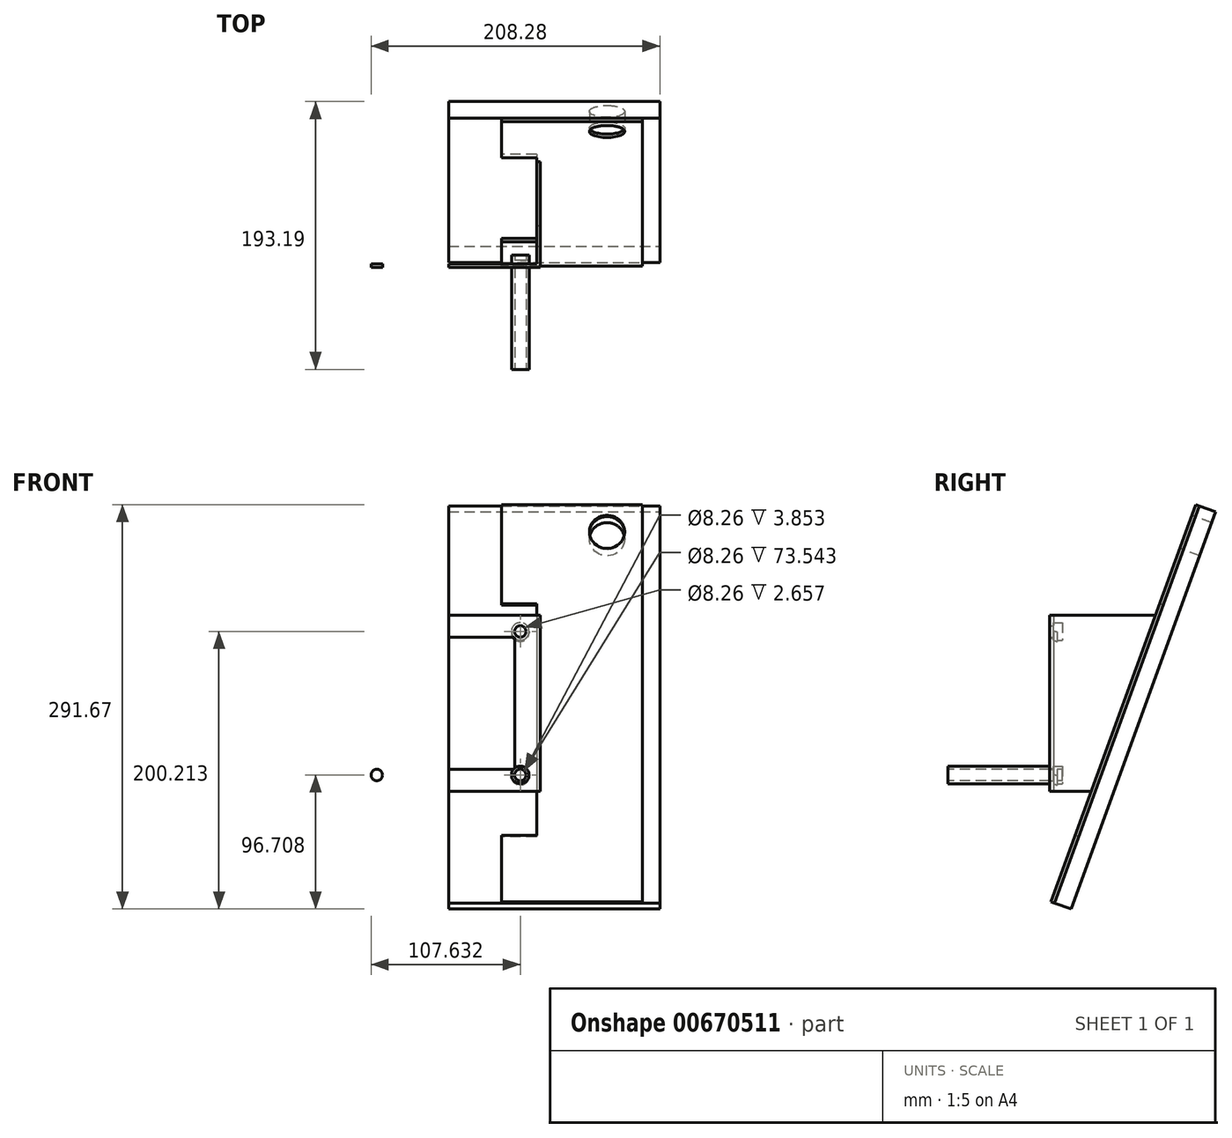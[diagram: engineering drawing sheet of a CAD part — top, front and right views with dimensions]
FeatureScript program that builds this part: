
annotation { "Feature Type Name" : "Feature", "Feature Type Description" : "" }
export const myFeature = defineFeature(function(context is Context, id is Id, definition is map)
    precondition{}
    {
        {
            var Q0;
            Q0=qCreatedBy(makeId("Front.planeOp"),FACE);
            var sketch = newSketch(context, id + "F0", { "sketchPlane" : qUnion([Q0])});
            skLineSegment(sketch, "E0.bottom", {"start": v(0, 63.5) * mm, "end": v(63.5, 63.5) * mm});
            skLineSegment(sketch, "E0.top", {"start": v(0, -63.5) * mm, "end": v(63.5, -63.5) * mm});
            skLineSegment(sketch, "E0.left", {"start": v(0, 63.5) * mm, "end": v(0, -63.5) * mm});
            skLineSegment(sketch, "E0.right", {"start": v(63.5, 63.5) * mm, "end": v(63.5, -63.5) * mm});
            skLineSegment(sketch, "E1.bottom", {"start": v(0, 47.62) * mm, "end": v(47.63, 47.62) * mm});
            skLineSegment(sketch, "E1.top", {"start": v(0, -47.62) * mm, "end": v(47.63, -47.62) * mm});
            skLineSegment(sketch, "E1.left", {"start": v(0, 47.62) * mm, "end": v(0, -47.62) * mm});
            skLineSegment(sketch, "E1.right", {"start": v(47.63, 47.62) * mm, "end": v(47.63, -47.62) * mm});
            skCircle(sketch, "E2", {"center": v(51.75, 51.75) * mm, "radius": 4.13 * mm});
            skCircle(sketch, "E3.MirrorC", {"center": v(51.75, -51.75) * mm, "radius": 4.13 * mm});
            skCircle(sketch, "E4", {"center": v(51.75, 51.75) * mm, "radius": 6.35 * mm});
            skCircle(sketch, "E5.MirrorC", {"center": v(51.75, -51.75) * mm, "radius": 6.35 * mm});
            skSolve(sketch);
        }
        {
            var Q0;
            Q0=makeQuery(id+"F0.imprint","IMPRINT",FACE,{"disambiguationData":[TD([[makeQuery(id+"F0.imprint","IMPRINT",EDGE,{"derivedFrom":sQuery(id+"F0.wireOp",EDGE,"E3.MirrorC")}),1.0]])]});
            var Q1;
            {var subQ5=sQuery(id+"F0.wireOp",EDGE,"E1.left");Q1=makeQuery(id+"F0.imprint","IMPRINT",FACE,{"disambiguationData":[TD([[makeQuery(id+"F0.imprint","IMPRINT",EDGE,{"derivedFrom":subQ5}),1.0]])]});}
            var Q2;
            {var subQ5=sQuery(id+"F0.wireOp",EDGE,"E0.bottom");Q2=makeQuery(id+"F0.imprint","IMPRINT",FACE,{"disambiguationData":[TD([[makeQuery(id+"F0.imprint","IMPRINT",EDGE,{"derivedFrom":subQ5}),-1.0]])]});}
            var Q3;
            Q3=makeQuery(id+"F0.imprint","IMPRINT",FACE,{"disambiguationData":[TD([[makeQuery(id+"F0.imprint","IMPRINT",EDGE,{"derivedFrom":sQuery(id+"F0.wireOp",EDGE,"E2")}),-1.0]])]});
            var Q4;
            {var subQ0=sQuery(id+"F0.wireOp",EDGE,"E1.right");var subQ1=sQuery(id+"F0.wireOp",EDGE,"E1.bottom");var subQ2=makeQuery(id+"F0.imprint","INTERSECT",VERTEX,{"derivedFrom":[subQ1,subQ0]});Q4=makeQuery(id+"F0.imprint","IMPRINT",FACE,{"disambiguationData":[TD([[makeQuery(id+"F0.imprint","IMPRINT",EDGE,{"disambiguationData":[TD([[subQ2,1.0]])],"derivedFrom":subQ1}),-1.0]])]});}
            var Q5;
            {var subQ0=sQuery(id+"F0.wireOp",EDGE,"E1.right");var subQ1=sQuery(id+"F0.wireOp",EDGE,"E1.top");var subQ2=makeQuery(id+"F0.imprint","INTERSECT",VERTEX,{"derivedFrom":[subQ1,subQ0]});Q5=makeQuery(id+"F0.imprint","IMPRINT",FACE,{"disambiguationData":[TD([[makeQuery(id+"F0.imprint","IMPRINT",EDGE,{"disambiguationData":[TD([[subQ2,1.0]])],"derivedFrom":subQ1}),1.0]])]});}
            extrude(context, id + "F1", {"entities" : qUnion([Q0, Q1, Q2, Q3, Q4, Q5]), "depth" : 2.66 * mm, "offsetDistance" : 25.4 * mm});
        }
        {
            var Q0;
            Q0=makeQuery(id+"F1.opExtrude","SWEPT_BODY",BODY,{"disambiguationData":[OSD([sQuery(id+"F0.wireOp",EDGE,"E0.bottom"),sQuery(id+"F0.wireOp",EDGE,"E0.top"),sQuery(id+"F0.wireOp",EDGE,"E0.left"),sQuery(id+"F0.wireOp",EDGE,"E0.right"),sQuery(id+"F0.wireOp",EDGE,"E1.left"),sQuery(id+"F0.wireOp",EDGE,"E2"),sQuery(id+"F0.wireOp",EDGE,"E3.MirrorC")])]});
            var Q1;
            Q1=qCreatedBy(makeId("Right.planeOp"),FACE);
            mirror(context, id + "F2", {"operationType" : NewBodyOperationType.ADD, "entities" : qUnion([Q0]), "mirrorPlane" : qUnion([Q1])});
        }
        {
            var Q0;
            Q0=makeQuery(id+"F1.opExtrude","SWEPT_FACE",FACE,{"disambiguationData":[OSD([sQuery(id+"F0.wireOp",EDGE,"E0.right")])]});
            var sketch = newSketch(context, id + "F3", { "sketchPlane" : qUnion([Q0])});
            skLineSegment(sketch, "E6", {"start": v(-2.66, -63.5) * mm, "end": v(-2.66, 63.5) * mm});
            skLineSegment(sketch, "E7", {"start": v(-2.66, 63.5) * mm, "end": v(73.54, 63.5) * mm});
            skLineSegment(sketch, "E8", {"start": v(73.54, 63.5) * mm, "end": v(27.32, -63.5) * mm});
            skLineSegment(sketch, "E9", {"start": v(27.32, -63.5) * mm, "end": v(-2.66, -63.5) * mm});
            skSolve(sketch);
        }
        {
            var Q0;
            Q0 = qSketchRegion(id + "F3", true);
            extrude(context, id + "F4", {"entities" : qUnion([Q0]), "operationType" : NewBodyOperationType.ADD, "depth" : 2.66 * mm, "offsetDistance" : 25.4 * mm});
        }
        {
            var Q0;
            Q0=makeQuery(id+"F1.opExtrude","CAP_FACE",FACE,{"disambiguationData":[OSD([sQuery(id+"F0.wireOp",EDGE,"E0.bottom"),sQuery(id+"F0.wireOp",EDGE,"E0.top"),sQuery(id+"F0.wireOp",EDGE,"E0.left"),sQuery(id+"F0.wireOp",EDGE,"E0.right"),sQuery(id+"F0.wireOp",EDGE,"E1.left"),sQuery(id+"F0.wireOp",EDGE,"E2"),sQuery(id+"F0.wireOp",EDGE,"E3.MirrorC")])],"isStart":true});
            var sketch = newSketch(context, id + "F5", { "sketchPlane" : qUnion([Q0])});
            skCircle(sketch, "E10", {"center": v(-51.75, 51.75) * mm, "radius": 6.35 * mm});
            skCircle(sketch, "E11.MirrorC", {"center": v(-51.75, -51.75) * mm, "radius": 6.35 * mm});
            skSolve(sketch);
        }
        {
            var Q0;
            Q0=makeQuery(id+"F5.imprint","IMPRINT",FACE,{"disambiguationData":[TD([[makeQuery(id+"F5.imprint","IMPRINT",EDGE,{"derivedFrom":sQuery(id+"F5.wireOp",EDGE,"E10")}),1.0]])]});
            var Q1;
            Q1=makeQuery(id+"F5.imprint","IMPRINT",FACE,{"disambiguationData":[TD([[makeQuery(id+"F5.imprint","IMPRINT",EDGE,{"derivedFrom":makeQuery(id+"F1.opExtrude","CAP_EDGE",EDGE,{"disambiguationData":[OSD([sQuery(id+"F0.wireOp",EDGE,"E2")])],"isStart":true})}),-1.0]])]});
            var Q2;
            Q2=makeQuery(id+"F5.imprint","IMPRINT",FACE,{"disambiguationData":[TD([[makeQuery(id+"F5.imprint","IMPRINT",EDGE,{"derivedFrom":sQuery(id+"F5.wireOp",EDGE,"E11.MirrorC")}),-1.0]])]});
            var Q3;
            Q3=makeQuery(id+"F5.imprint","IMPRINT",FACE,{"disambiguationData":[TD([[makeQuery(id+"F5.imprint","IMPRINT",EDGE,{"derivedFrom":makeQuery(id+"F1.opExtrude","CAP_EDGE",EDGE,{"disambiguationData":[OSD([sQuery(id+"F0.wireOp",EDGE,"E3.MirrorC")])],"isStart":true})}),1.0]])]});
            var Q4;
            Q4=sQuery(id+"F5.wireOp",EDGE,"E10");
            var Q5;
            Q5=sQuery(id+"F5.wireOp",EDGE,"E11.MirrorC");
            extrude(context, id + "F6", {"entities" : qUnion([Q0, Q1, Q2, Q3]), "surfaceEntities" : qUnion([Q4, Q5]), "depth" : 6.35 * mm, "offsetDistance" : 25.4 * mm});
        }
        {
            var Q0;
            Q0=makeQuery(id+"F5.imprint","IMPRINT",FACE,{"disambiguationData":[TD([[makeQuery(id+"F5.imprint","IMPRINT",EDGE,{"derivedFrom":makeQuery(id+"F1.opExtrude","CAP_EDGE",EDGE,{"disambiguationData":[OSD([sQuery(id+"F0.wireOp",EDGE,"E2")])],"isStart":true})}),-1.0]])]});
            var Q1;
            Q1=makeQuery(id+"F5.imprint","IMPRINT",FACE,{"disambiguationData":[TD([[makeQuery(id+"F5.imprint","IMPRINT",EDGE,{"derivedFrom":makeQuery(id+"F1.opExtrude","CAP_EDGE",EDGE,{"disambiguationData":[OSD([sQuery(id+"F0.wireOp",EDGE,"E3.MirrorC")])],"isStart":true})}),1.0]])]});
            extrude(context, id + "F7", {"entities" : qUnion([Q0, Q1]), "operationType" : NewBodyOperationType.ADD, "oppositeDirection" : true, "depth" : 76.2 * mm, "offsetDistance" : 25.4 * mm});
        }
        {
            var Q0;
            Q0=makeQuery(id+"F4.opExtrude","SWEPT_FACE",FACE,{"disambiguationData":[OSD([sQuery(id+"F3.wireOp",EDGE,"E8")])]});
            var sketch = newSketch(context, id + "F8", { "sketchPlane" : qUnion([Q0])});
            skLineSegment(sketch, "E12.bottom", {"start": v(-139.7, 169.65) * mm, "end": v(-63.5, 169.65) * mm});
            skLineSegment(sketch, "E12.top", {"start": v(-139.7, -135.15) * mm, "end": v(-63.5, -135.15) * mm});
            skLineSegment(sketch, "E12.left", {"start": v(-139.7, 169.65) * mm, "end": v(-139.7, -135.15) * mm});
            skLineSegment(sketch, "E12.right", {"start": v(-63.5, 169.65) * mm, "end": v(-63.5, -135.15) * mm});
            skLineSegment(sketch, "E13.bottom", {"start": v(-63.5, 169.65) * mm, "end": v(-38.1, 169.65) * mm});
            skLineSegment(sketch, "E13.top", {"start": v(-63.5, 93.45) * mm, "end": v(-38.1, 93.45) * mm});
            skLineSegment(sketch, "E13.left", {"start": v(-63.5, 169.65) * mm, "end": v(-63.5, 93.45) * mm});
            skLineSegment(sketch, "E13.right", {"start": v(-38.1, 169.65) * mm, "end": v(-38.1, 93.45) * mm});
            skLineSegment(sketch, "E14.bottom", {"start": v(-63.5, -135.15) * mm, "end": v(-38.1, -135.15) * mm});
            skLineSegment(sketch, "E14.top", {"start": v(-63.5, -84.35) * mm, "end": v(-38.1, -84.35) * mm});
            skLineSegment(sketch, "E14.left", {"start": v(-63.5, -135.15) * mm, "end": v(-63.5, -84.35) * mm});
            skLineSegment(sketch, "E14.right", {"start": v(-38.1, -135.15) * mm, "end": v(-38.1, -84.35) * mm});
            skCircle(sketch, "E15", {"center": v(-114.3, 148.7) * mm, "radius": 12.7 * mm});
            skSolve(sketch);
        }
        {
            var Q0;
            Q0 = qSketchRegion(id + "F8", true);
            var Q1;
            Q1 = qSketchRegion(id + "F5", true);
            extrude(context, id + "F9", {"entities" : qUnion([Q0, Q1]), "operationType" : NewBodyOperationType.ADD, "depth" : 2.66 * mm, "offsetDistance" : 25.4 * mm});
        }
        {
            var Q0;
            Q0=makeQuery(id+"F9.opExtrude","CAP_FACE",FACE,{"disambiguationData":[OSD([sQuery(id+"F8.wireOp",EDGE,"E12.bottom"),sQuery(id+"F8.wireOp",EDGE,"E12.top"),sQuery(id+"F8.wireOp",EDGE,"E12.left"),sQuery(id+"F8.wireOp",EDGE,"E12.right"),sQuery(id+"F8.wireOp",EDGE,"E13.bottom"),sQuery(id+"F8.wireOp",EDGE,"E13.top"),sQuery(id+"F8.wireOp",EDGE,"E13.right"),sQuery(id+"F8.wireOp",EDGE,"E14.bottom"),sQuery(id+"F8.wireOp",EDGE,"E14.top"),sQuery(id+"F8.wireOp",EDGE,"E14.right"),sQuery(id+"F8.wireOp",EDGE,"E15")])],"isStart":false});
            var sketch = newSketch(context, id + "F10", { "sketchPlane" : qUnion([Q0])});
            skLineSegment(sketch, "E16.bottom", {"start": v(0, -135.15) * mm, "end": v(-152.4, -135.15) * mm});
            skLineSegment(sketch, "E16.top", {"start": v(0, 169.65) * mm, "end": v(-152.4, 169.65) * mm});
            skLineSegment(sketch, "E16.left", {"start": v(0, -135.15) * mm, "end": v(0, 169.65) * mm});
            skLineSegment(sketch, "E16.right", {"start": v(-152.4, -135.15) * mm, "end": v(-152.4, 169.65) * mm});
            skPoint(sketch, "E16.middle", {"position": v(-76.2, 17.25) * mm});
            skCircle(sketch, "E17", {"center": v(-114.3, 148.7) * mm, "radius": 12.7 * mm});
            skSolve(sketch);
        }
        {
            var Q0;
            Q0 = qSketchRegion(id + "F10", true);
            extrude(context, id + "F11", {"entities" : qUnion([Q0]), "depth" : 12.7 * mm, "offsetDistance" : 25.4 * mm});
        }
    });
